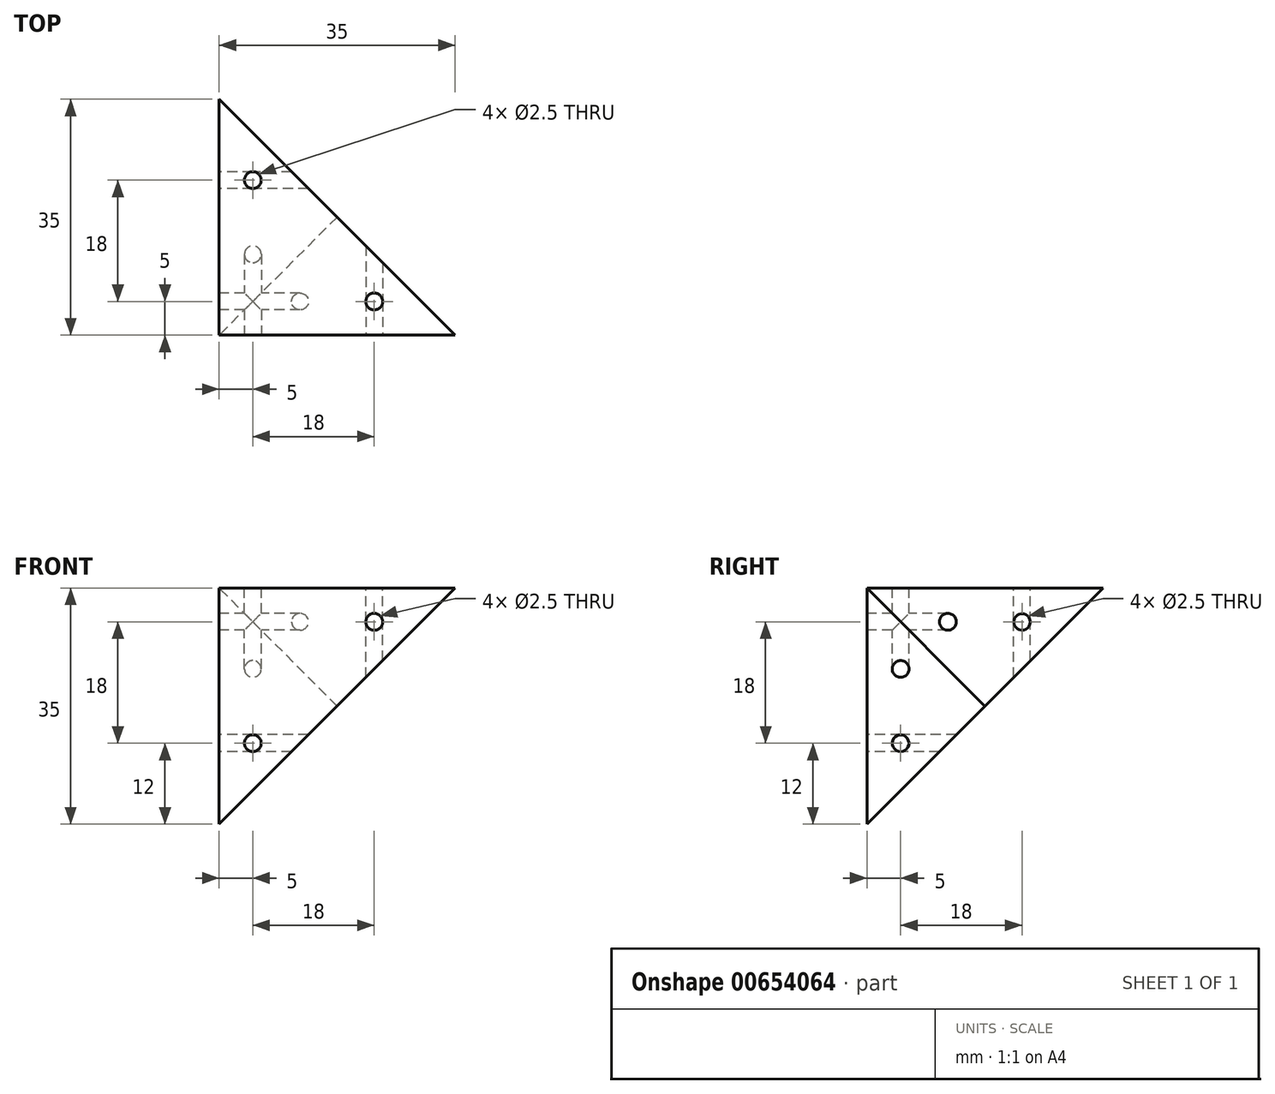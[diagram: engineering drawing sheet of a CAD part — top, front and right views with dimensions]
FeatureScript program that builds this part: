
annotation { "Feature Type Name" : "Feature", "Feature Type Description" : "" }
export const myFeature = defineFeature(function(context is Context, id is Id, definition is map)
    precondition{}
    {
        {
            var Q0;
            Q0=qCreatedBy(makeId("Top.planeOp"),FACE);
            var sketch = newSketch(context, id + "F0", { "sketchPlane" : qUnion([Q0])});
            skLineSegment(sketch, "E0.bottom", {"start": v(0, 0) * mm, "end": v(35, 0) * mm});
            skLineSegment(sketch, "E0.top", {"start": v(0, 35) * mm, "end": v(35, 35) * mm});
            skLineSegment(sketch, "E0.left", {"start": v(0, 0) * mm, "end": v(0, 35) * mm});
            skLineSegment(sketch, "E0.right", {"start": v(35, 0) * mm, "end": v(35, 35) * mm});
            skSolve(sketch);
        }
        {
            var Q0;
            Q0=makeQuery(id+"F0.imprint","IMPRINT",FACE,{"disambiguationData":[TD([[makeQuery(id+"F0.imprint","IMPRINT",EDGE,{"derivedFrom":sQuery(id+"F0.wireOp",EDGE,"E0.bottom")}),1.0]])]});
            extrude(context, id + "F1", {"entities" : qUnion([Q0]), "depth" : 35 * mm, "offsetDistance" : 25 * mm});
        }
        {
            var Q0;
            Q0=makeQuery(id+"F1.opExtrude","CAP_FACE",FACE,{"disambiguationData":[OSD([sQuery(id+"F0.wireOp",EDGE,"E0.bottom"),sQuery(id+"F0.wireOp",EDGE,"E0.top"),sQuery(id+"F0.wireOp",EDGE,"E0.left"),sQuery(id+"F0.wireOp",EDGE,"E0.right")])],"isStart":false});
            var sketch = newSketch(context, id + "F2", { "sketchPlane" : qUnion([Q0])});
            skLineSegment(sketch, "E1", {"start": v(0, 35) * mm, "end": v(35, 0) * mm});
            skSolve(sketch);
        }
        {
            var Q0;
            Q0=makeQuery(id+"F2.imprint","IMPRINT",FACE,{"disambiguationData":[TD([[makeQuery(id+"F2.imprint","IMPRINT",EDGE,{"derivedFrom":sQuery(id+"F2.wireOp",EDGE,"E1")}),1.0]])]});
            extrude(context, id + "F3", {"entities" : qUnion([Q0]), "operationType" : NewBodyOperationType.REMOVE, "endBound" : BoundingType.THROUGH_ALL, "oppositeDirection" : true, "depth" : 25 * mm, "offsetDistance" : 25 * mm});
        }
        {
            var Q0;
            Q0=makeQuery(id+"F1.opExtrude","SWEPT_FACE",FACE,{"disambiguationData":[OSD([sQuery(id+"F0.wireOp",EDGE,"E0.bottom")])]});
            var sketch = newSketch(context, id + "F4", { "sketchPlane" : qUnion([Q0])});
            skLineSegment(sketch, "E2", {"start": v(0, 0) * mm, "end": v(35, 35) * mm});
            skSolve(sketch);
        }
        {
            var Q0;
            Q0=makeQuery(id+"F4.imprint","IMPRINT",FACE,{"disambiguationData":[TD([[makeQuery(id+"F4.imprint","IMPRINT",EDGE,{"derivedFrom":sQuery(id+"F4.wireOp",EDGE,"E2")}),-1.0]])]});
            extrude(context, id + "F5", {"entities" : qUnion([Q0]), "operationType" : NewBodyOperationType.REMOVE, "endBound" : BoundingType.THROUGH_ALL, "oppositeDirection" : true, "depth" : 25 * mm, "offsetDistance" : 25 * mm});
        }
        {
            var Q0;
            Q0=makeQuery(id+"F1.opExtrude","SWEPT_FACE",FACE,{"disambiguationData":[OSD([sQuery(id+"F0.wireOp",EDGE,"E0.left")])]});
            var sketch = newSketch(context, id + "F6", { "sketchPlane" : qUnion([Q0])});
            skLineSegment(sketch, "E3", {"start": v(0, 0) * mm, "end": v(-35, 35) * mm});
            skSolve(sketch);
        }
        {
            var Q0;
            Q0=makeQuery(id+"F6.imprint","IMPRINT",FACE,{"disambiguationData":[TD([[makeQuery(id+"F6.imprint","IMPRINT",EDGE,{"derivedFrom":sQuery(id+"F6.wireOp",EDGE,"E3")}),1.0]])]});
            extrude(context, id + "F7", {"entities" : qUnion([Q0]), "operationType" : NewBodyOperationType.REMOVE, "endBound" : BoundingType.THROUGH_ALL, "oppositeDirection" : true, "depth" : 25 * mm, "offsetDistance" : 25 * mm});
        }
        {
            var Q0;
            Q0=makeQuery(id+"F1.opExtrude","SWEPT_FACE",FACE,{"disambiguationData":[OSD([sQuery(id+"F0.wireOp",EDGE,"E0.bottom")])]});
            var sketch = newSketch(context, id + "F8", { "sketchPlane" : qUnion([Q0])});
            skPoint(sketch, "E4", {"position": v(5, 12) * mm});
            skPoint(sketch, "E5", {"position": v(23, 30) * mm});
            skSolve(sketch);
        }
        {
            var Q0;
            Q0=sQuery(id+"F8.wireOp",VERTEX,"E5");
            var Q1;
            Q1=sQuery(id+"F8.wireOp",VERTEX,"E4");
            var Q2;
            Q2=makeQuery(id+"F1.opExtrude","SWEPT_BODY",BODY,{"disambiguationData":[OSD([sQuery(id+"F0.wireOp",EDGE,"E0.bottom"),sQuery(id+"F0.wireOp",EDGE,"E0.top"),sQuery(id+"F0.wireOp",EDGE,"E0.left"),sQuery(id+"F0.wireOp",EDGE,"E0.right")])]});
            hole(context, id + "F9", {"style" : HoleStyle.SIMPLE, "endStyle" : HoleEndStyle.THROUGH, "standardTappedOrClearance" : lookupTablePath({ "standard" : "ISO", "engagement" : "75%", "pitch" : "0.5 mm", "size" : "M3", "type" : "Tapped" }), "standardBlindInLast" : lookupTablePath({ "standard" : "ISO", "engagement" : "75%", "pitch" : "0.5 mm", "size" : "M3", "type" : "Tapped" }), "holeDiameter" : 2.5 * mm, "majorDiameter" : 3 * mm, "showTappedDepth" : true, "isTappedThrough" : true, "tappedDepth" : 5 * mm, "tapClearance" : 3, "startFromSketch" : true, "locations" : qUnion([Q0, Q1]), "scope" : qUnion([Q2])});
        }
        {
            var Q0;
            Q0=makeQuery(id+"F1.opExtrude","SWEPT_FACE",FACE,{"disambiguationData":[OSD([sQuery(id+"F0.wireOp",EDGE,"E0.left")])]});
            var sketch = newSketch(context, id + "F10", { "sketchPlane" : qUnion([Q0])});
            skPoint(sketch, "E6", {"position": v(-23, 30) * mm});
            skPoint(sketch, "E7", {"position": v(-5, 12) * mm});
            skSolve(sketch);
        }
        {
            var Q0;
            Q0=sQuery(id+"F10.wireOp",VERTEX,"E6");
            var Q1;
            Q1=sQuery(id+"F10.wireOp",VERTEX,"E7");
            var Q2;
            Q2=makeQuery(id+"F1.opExtrude","SWEPT_BODY",BODY,{"disambiguationData":[OSD([sQuery(id+"F0.wireOp",EDGE,"E0.bottom"),sQuery(id+"F0.wireOp",EDGE,"E0.top"),sQuery(id+"F0.wireOp",EDGE,"E0.left"),sQuery(id+"F0.wireOp",EDGE,"E0.right")])]});
            hole(context, id + "F11", {"style" : HoleStyle.SIMPLE, "endStyle" : HoleEndStyle.THROUGH, "standardTappedOrClearance" : lookupTablePath({ "standard" : "ISO", "engagement" : "75%", "pitch" : "0.5 mm", "size" : "M3", "type" : "Tapped" }), "standardBlindInLast" : lookupTablePath({ "standard" : "ISO", "engagement" : "75%", "pitch" : "0.5 mm", "size" : "M3", "type" : "Tapped" }), "holeDiameter" : 2.5 * mm, "majorDiameter" : 3 * mm, "showTappedDepth" : true, "isTappedThrough" : true, "tappedDepth" : 5 * mm, "tapClearance" : 3, "startFromSketch" : true, "locations" : qUnion([Q0, Q1]), "scope" : qUnion([Q2])});
        }
        {
            var Q0;
            Q0=makeQuery(id+"F1.opExtrude","CAP_FACE",FACE,{"disambiguationData":[OSD([sQuery(id+"F0.wireOp",EDGE,"E0.bottom"),sQuery(id+"F0.wireOp",EDGE,"E0.top"),sQuery(id+"F0.wireOp",EDGE,"E0.left"),sQuery(id+"F0.wireOp",EDGE,"E0.right")])],"isStart":false});
            var sketch = newSketch(context, id + "F12", { "sketchPlane" : qUnion([Q0])});
            skPoint(sketch, "E8", {"position": v(5, 23) * mm});
            skPoint(sketch, "E9", {"position": v(23, 5) * mm});
            skSolve(sketch);
        }
        {
            var Q0;
            Q0=sQuery(id+"F12.wireOp",VERTEX,"E8");
            var Q1;
            Q1=sQuery(id+"F12.wireOp",VERTEX,"E9");
            var Q2;
            Q2=makeQuery(id+"F1.opExtrude","SWEPT_BODY",BODY,{"disambiguationData":[OSD([sQuery(id+"F0.wireOp",EDGE,"E0.bottom"),sQuery(id+"F0.wireOp",EDGE,"E0.top"),sQuery(id+"F0.wireOp",EDGE,"E0.left"),sQuery(id+"F0.wireOp",EDGE,"E0.right")])]});
            hole(context, id + "F13", {"style" : HoleStyle.SIMPLE, "endStyle" : HoleEndStyle.THROUGH, "standardTappedOrClearance" : lookupTablePath({ "standard" : "ISO", "engagement" : "75%", "pitch" : "0.5 mm", "size" : "M3", "type" : "Tapped" }), "standardBlindInLast" : lookupTablePath({ "standard" : "ISO", "engagement" : "75%", "pitch" : "0.5 mm", "size" : "M3", "type" : "Tapped" }), "holeDiameter" : 2.5 * mm, "majorDiameter" : 3 * mm, "showTappedDepth" : true, "isTappedThrough" : true, "tappedDepth" : 5 * mm, "tapClearance" : 3, "startFromSketch" : true, "locations" : qUnion([Q0, Q1]), "scope" : qUnion([Q2])});
        }
    });
